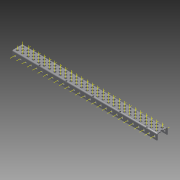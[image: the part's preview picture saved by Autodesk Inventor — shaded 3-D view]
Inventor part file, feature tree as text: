
AUTODESK INVENTOR PART (.ipt)
format: ipt  version: 2015 SP1 (Build 190203100, 203)  size: 2,128,384 bytes
history: native  units: in
note: dims shown in document units (in); Inventor stores cm internally (conversion verified against a paired STEP export)
features: other x141, pattern_linear x3, sheet_metal_op x1, extrude x1, imported_body x1, sketch x1
ambient origin geometry x8: Origin, YZ Plane, XZ Plane, XY Plane, X Axis, Y Axis, Z Axis, Center Point
bodies: Body1 (feature_tree)
feature tree (148):
  sheet_metal_op  "Fold1"
  other  "C-Channel"
  extrude  "length cut"  Depth=0.5in
  other  "top axis"
  other  "inner axis"
  other  "front axis"
  other  "back axis"
  pattern_linear  "top axes"  Spacing1=0.5in  [1 undecoded]
  pattern_linear  "inner axes"  Spacing1=0.5in  [1 undecoded]
  pattern_linear  "horiz axes"  Spacing1=-13.5in  [1 undecoded]
  other  "right plane"
  imported_body  "Base1"
  sketch  "Sketch1"  dims[d1=0.0in d4=0.5in d5=0.7874in d7=0.5in d10=0.5in d13=0.5in d14=-13.5in d15=0.0in d16=0.0in d17=0.0in d18=0.0in d19=0.0in]
  other  "Work Point1"
  other  "Work Point2"
  other  "Work Point3"
  other  "Work Point4"
  other  "Work Axis5"
  other  "Work Axis6"
  other  "Work Axis7"
  other  "Work Axis8"
  other  "Work Axis11"
  other  "Work Axis12"
  other  "Work Axis13"
  other  "Work Axis14"
  other  "Work Axis15"
  other  "Work Axis18"
  other  "Work Axis19"
  other  "Work Axis20"
  other  "Work Axis23"
  other  "Work Axis24"
  other  "Work Axis25"
  other  "Work Axis26"
  other  "Work Axis30"
  other  "Work Axis31"
  other  "Work Axis32"
  other  "Work Axis33"
  other  "left plane"
  other  "Work Axis37"
  other  "Work Axis38"
  other  "Work Axis39"
  other  "Work Axis40"
  other  "Work Axis41"
  other  "Work Axis42"
  other  "Work Axis43"
  other  "Work Axis44"
  other  "Work Axis45"
  other  "Work Axis46"
  other  "Work Axis47"
  other  "Work Axis48"
  other  "Work Axis49"
  other  "Work Axis50"
  other  "Work Axis51"
  other  "Work Axis52"
  other  "Work Axis53"
  other  "Work Axis54"
  other  "Work Axis55"
  other  "Work Axis56"
  other  "Work Axis57"
  other  "Work Axis58"
  other  "Work Axis59"
  other  "Work Axis60"
  other  "Work Axis61"
  other  "Work Axis62"
  other  "Work Axis63"
  other  "Work Axis64"
  other  "Work Axis65"
  other  "Work Axis66"
  other  "Work Axis67"
  other  "Work Axis68"
  other  "Work Axis69"
  other  "Work Axis70"
  other  "Work Axis71"
  other  "Work Axis72"
  other  "Work Axis73"
  other  "Work Axis74"
  other  "Work Axis75"
  other  "Work Axis76"
  other  "Work Axis77"
  other  "Work Axis78"
  other  "Work Axis79"
  other  "Work Axis80"
  other  "Work Axis81"
  other  "Work Axis82"
  other  "Work Axis83"
  other  "Work Axis84"
  other  "Work Axis85"
  other  "Work Axis86"
  other  "Work Axis87"
  other  "Work Axis88"
  other  "Work Axis89"
  other  "Work Axis90"
  other  "Work Axis91"
  other  "Work Axis92"
  other  "Work Axis93"
  other  "Work Axis94"
  other  "Work Axis95"
  other  "Work Axis96"
  other  "Work Axis97"
  other  "Work Axis98"
  other  "Work Axis99"
  other  "Work Axis100"
  other  "Work Axis101"
  other  "Work Axis102"
  other  "Work Axis103"
  other  "Work Axis104"
  other  "Work Axis105"
  other  "Work Axis106"
  other  "Work Axis107"
  other  "Work Axis108"
  other  "Work Axis109"
  other  "Work Axis110"
  other  "Work Axis111"
  other  "Work Axis112"
  other  "Work Axis113"
  other  "Work Axis114"
  other  "Work Axis115"
  other  "Work Axis116"
  other  "Work Axis117"
  other  "Work Axis118"
  other  "Work Axis119"
  other  "Work Axis120"
  other  "Work Axis121"
  other  "Work Axis122"
  other  "Work Axis123"
  other  "Work Axis124"
  other  "Work Axis125"
  other  "Work Axis126"
  other  "Work Axis127"
  other  "Work Axis128"
  other  "Work Axis129"
  other  "Work Axis130"
  other  "Work Axis131"
  other  "Work Axis132"
  other  "Work Axis133"
  other  "Work Axis134"
  other  "Work Axis135"
  other  "Work Axis136"
  other  "Work Axis137"
  other  "Work Axis138"
  other  "Work Axis140"
  other  "Work Axis141"
  other  "Work Axis143"
  other  "Work Axis144"
  other  "Work Axis146"
  other  "Work Axis147"
  other  "Work Axis149"
  other  "Work Axis150"
note: 3 required parameter values undecoded (feature->parameter linkage not recoverable at this tier; creation-order binding heuristic only, values carry confidence <= 0.55)
